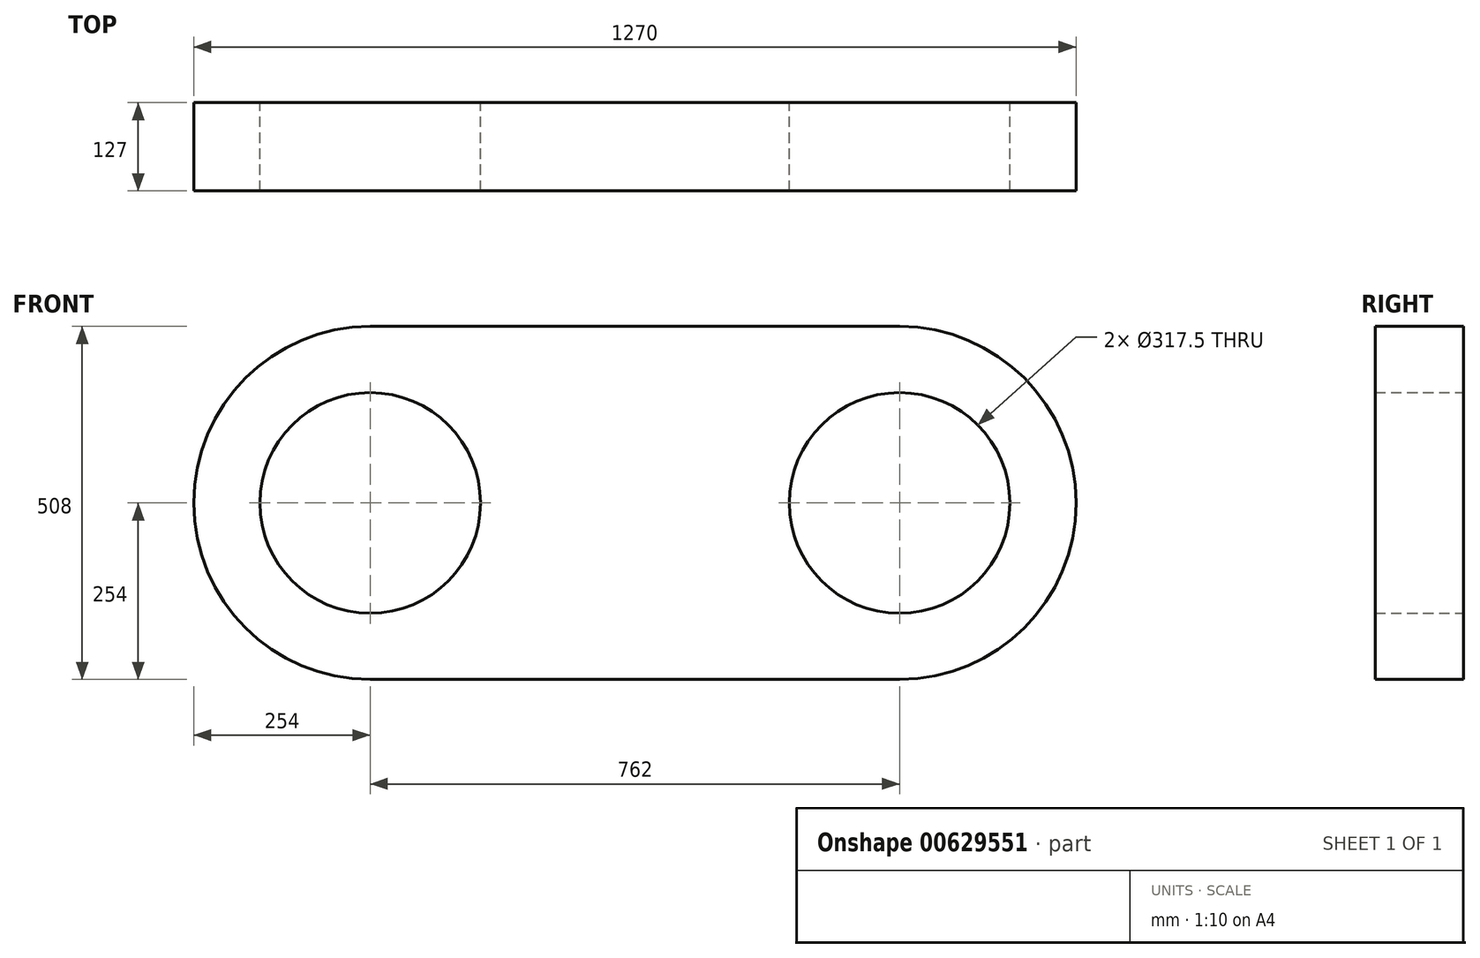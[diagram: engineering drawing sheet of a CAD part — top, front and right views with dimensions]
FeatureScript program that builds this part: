
annotation { "Feature Type Name" : "Feature", "Feature Type Description" : "" }
export const myFeature = defineFeature(function(context is Context, id is Id, definition is map)
    precondition{}
    {
        {
            var Q0;
            Q0=qCreatedBy(makeId("Front.planeOp"),FACE);
            var sketch = newSketch(context, id + "F0", { "sketchPlane" : qUnion([Q0])});
            skLineSegment(sketch, "E0.bottom", {"start": v(-381, 254) * mm, "end": v(381, 254) * mm});
            skLineSegment(sketch, "E0.top", {"start": v(-381, -254) * mm, "end": v(381, -254) * mm});
            skArc(sketch, "E1", {"start": v(-381, 254) * mm, "mid": v(-635, 0) * mm, "end": v(-381, -254) * mm});
            skArc(sketch, "E2", {"start": v(381, -254) * mm, "mid": v(635, 0) * mm, "end": v(381, 254) * mm});
            skCircle(sketch, "E3", {"center": v(-381, 0) * mm, "radius": 158.75 * mm});
            skCircle(sketch, "E4", {"center": v(381, 0) * mm, "radius": 158.75 * mm});
            skSolve(sketch);
        }
        {
            var Q0;
            Q0 = qSketchRegion(id + "F0", true);
            extrude(context, id + "F1", {"entities" : qUnion([Q0]), "depth" : 127 * mm, "offsetDistance" : 25.4 * mm});
        }
    });
